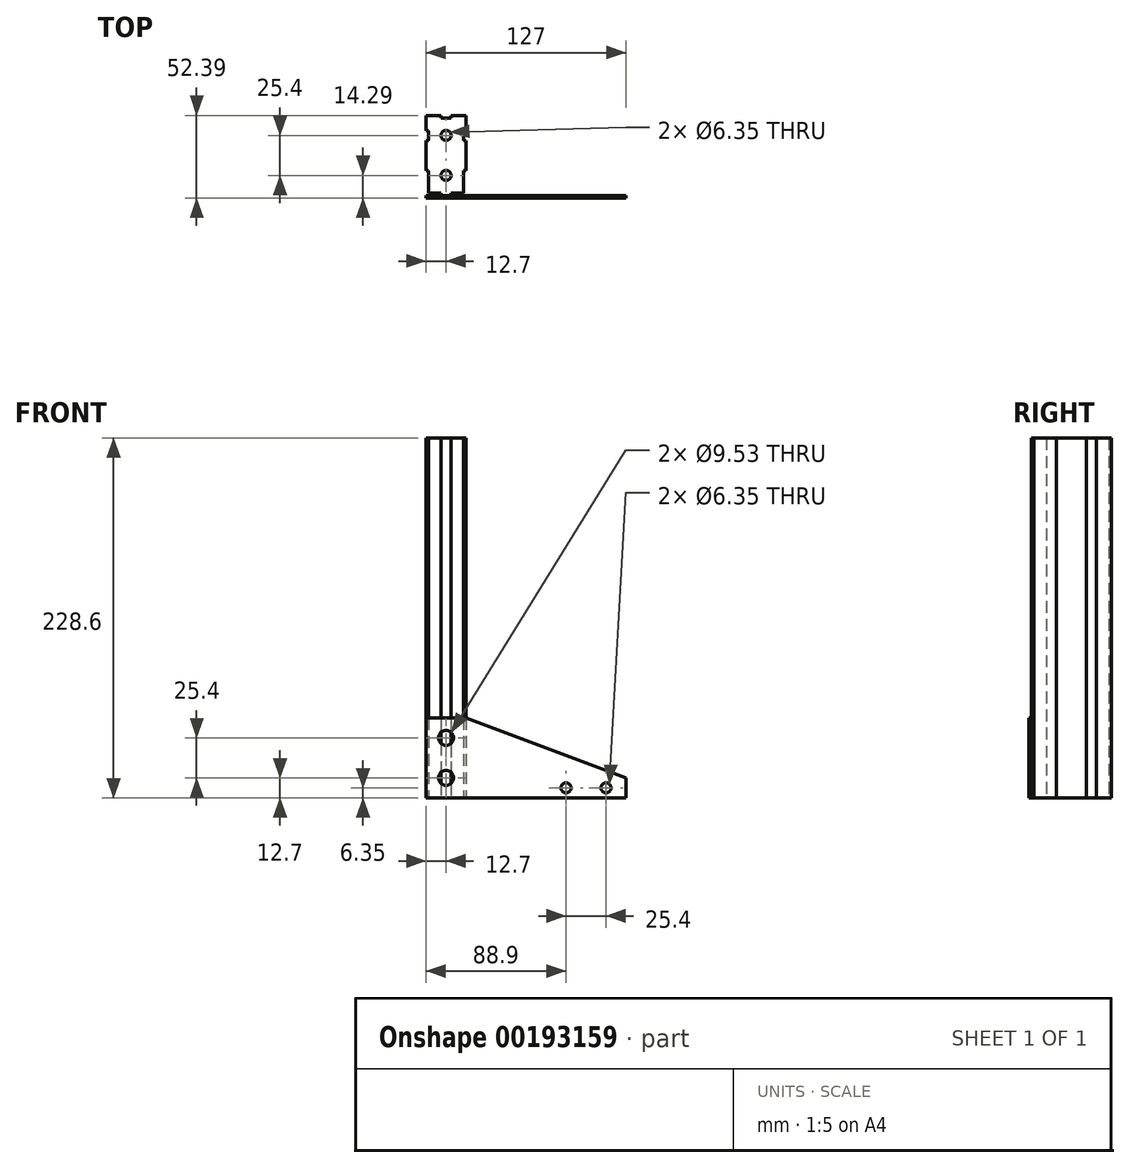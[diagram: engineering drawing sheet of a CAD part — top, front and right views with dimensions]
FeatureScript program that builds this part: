
annotation { "Feature Type Name" : "Feature", "Feature Type Description" : "" }
export const myFeature = defineFeature(function(context is Context, id is Id, definition is map)
    precondition{}
    {
        {
            var Q0;
            Q0=qCreatedBy(makeId("Top.planeOp"),FACE);
            var sketch = newSketch(context, id + "F0", { "sketchPlane" : qUnion([Q0])});
            skLineSegment(sketch, "E0.bottom", {"start": v(-12.7, -25.4) * mm, "end": v(12.7, -25.4) * mm});
            skLineSegment(sketch, "E0.top", {"start": v(-12.7, 25.4) * mm, "end": v(12.7, 25.4) * mm});
            skLineSegment(sketch, "E0.left", {"start": v(-12.7, -25.4) * mm, "end": v(-12.7, 25.4) * mm});
            skLineSegment(sketch, "E0.right", {"start": v(12.7, -25.4) * mm, "end": v(12.7, 25.4) * mm});
            skPoint(sketch, "E0.middle", {"position": v(0, 0) * mm});
            skLineSegment(sketch, "E1", {"start": v(12.7, 0) * mm, "end": v(88.9, 0) * mm, "construction": true});
            skPoint(sketch, "E1.endSnap0", {"position": v(12.7, 0) * mm});
            skLineSegment(sketch, "E2", {"start": v(88.9, 0) * mm, "end": v(114.3, 0) * mm, "construction": true});
            skLineSegment(sketch, "E3.bottom", {"start": v(79.38, -9.53) * mm, "end": v(98.42, -9.53) * mm});
            skLineSegment(sketch, "E3.top", {"start": v(79.38, 9.52) * mm, "end": v(98.42, 9.52) * mm});
            skLineSegment(sketch, "E3.left", {"start": v(79.38, -9.53) * mm, "end": v(79.38, 9.52) * mm});
            skLineSegment(sketch, "E3.right", {"start": v(98.42, -9.53) * mm, "end": v(98.42, 9.52) * mm});
            skPoint(sketch, "E3.middle", {"position": v(88.9, 0) * mm});
            skLineSegment(sketch, "E4.bottom", {"start": v(63.5, -25.4) * mm, "end": v(114.3, -25.4) * mm});
            skLineSegment(sketch, "E4.top", {"start": v(63.5, 25.4) * mm, "end": v(114.3, 25.4) * mm});
            skLineSegment(sketch, "E4.left", {"start": v(63.5, -25.4) * mm, "end": v(63.5, 25.4) * mm});
            skLineSegment(sketch, "E4.right", {"start": v(114.3, -25.4) * mm, "end": v(114.3, 25.4) * mm});
            skLineSegment(sketch, "E5", {"start": v(-12.7, 0) * mm, "end": v(12.7, 0) * mm});
            skLineSegment(sketch, "E6", {"start": v(0, 25.4) * mm, "end": v(0, 0) * mm});
            skLineSegment(sketch, "E7", {"start": v(0, 0) * mm, "end": v(0, -25.4) * mm});
            skCircle(sketch, "E8", {"center": v(0, 12.7) * mm, "radius": 3.18 * mm});
            skCircle(sketch, "E9", {"center": v(0, -12.7) * mm, "radius": 3.18 * mm});
            skLineSegment(sketch, "E10.bottom", {"start": v(-11.11, 1.59) * mm, "end": v(11.11, 1.59) * mm});
            skLineSegment(sketch, "E10.top", {"start": v(-11.11, 23.81) * mm, "end": v(11.11, 23.81) * mm});
            skLineSegment(sketch, "E10.left", {"start": v(-11.11, 1.59) * mm, "end": v(-11.11, 23.81) * mm});
            skLineSegment(sketch, "E10.right", {"start": v(11.11, 1.59) * mm, "end": v(11.11, 23.81) * mm});
            skLineSegment(sketch, "E11.bottom", {"start": v(-11.11, -23.81) * mm, "end": v(11.11, -23.81) * mm});
            skLineSegment(sketch, "E11.top", {"start": v(-11.11, -1.59) * mm, "end": v(11.11, -1.59) * mm});
            skLineSegment(sketch, "E11.left", {"start": v(-11.11, -23.81) * mm, "end": v(-11.11, -1.59) * mm});
            skLineSegment(sketch, "E11.right", {"start": v(11.11, -23.81) * mm, "end": v(11.11, -1.59) * mm});
            skLineSegment(sketch, "E12.bottom", {"start": v(-3.18, -25.4) * mm, "end": v(3.18, -25.4) * mm});
            skLineSegment(sketch, "E12.top", {"start": v(-3.18, 25.4) * mm, "end": v(3.18, 25.4) * mm});
            skLineSegment(sketch, "E12.left", {"start": v(-3.18, -25.4) * mm, "end": v(-3.18, 25.4) * mm});
            skLineSegment(sketch, "E12.right", {"start": v(3.18, -25.4) * mm, "end": v(3.18, 25.4) * mm});
            skLineSegment(sketch, "E13.bottom", {"start": v(-12.7, 9.53) * mm, "end": v(12.7, 9.53) * mm});
            skLineSegment(sketch, "E13.top", {"start": v(-12.7, 15.88) * mm, "end": v(12.7, 15.88) * mm});
            skLineSegment(sketch, "E13.left", {"start": v(-12.7, 9.53) * mm, "end": v(-12.7, 15.88) * mm});
            skLineSegment(sketch, "E13.right", {"start": v(12.7, 9.53) * mm, "end": v(12.7, 15.88) * mm});
            skLineSegment(sketch, "E14.MirrorCS", {"start": v(12.7, -9.53) * mm, "end": v(12.7, -15.88) * mm});
            skLineSegment(sketch, "E15.MirrorCS", {"start": v(-12.7, -9.52) * mm, "end": v(12.7, -9.53) * mm});
            skLineSegment(sketch, "E16.MirrorCS", {"start": v(-12.7, -15.88) * mm, "end": v(12.7, -15.88) * mm});
            skLineSegment(sketch, "E17.MirrorCS", {"start": v(-12.7, -9.52) * mm, "end": v(-12.7, -15.88) * mm});
            skSolve(sketch);
        }
        {
            var Q0;
            Q0=makeQuery(id+"F0.imprint","IMPRINT",FACE,{"disambiguationData":[TD([[makeQuery(id+"F0.imprint","IMPRINT",EDGE,{"derivedFrom":sQuery(id+"F0.wireOp",EDGE,"E0.bottom")}),1.0]])]});
            var Q1;
            {var subQ7=sQuery(id+"F0.wireOp",EDGE,"E5");var subQ8=sQuery(id+"F0.wireOp",EDGE,"E0.right");var subQ9=makeQuery(id+"F0.imprint","INTERSECT",VERTEX,{"derivedFrom":[subQ8,subQ7]});Q1=makeQuery(id+"F0.imprint","IMPRINT",FACE,{"disambiguationData":[TD([[makeQuery(id+"F0.imprint","IMPRINT",EDGE,{"disambiguationData":[TD([[subQ9,1.0]])],"derivedFrom":subQ7}),-1.0]])]});}
            var Q2;
            {var subQ6=sQuery(id+"F0.wireOp",EDGE,"E5");var subQ9=sQuery(id+"F0.wireOp",EDGE,"E0.left");var subQ10=makeQuery(id+"F0.imprint","INTERSECT",VERTEX,{"derivedFrom":[subQ9,subQ6]});Q2=makeQuery(id+"F0.imprint","IMPRINT",FACE,{"disambiguationData":[TD([[makeQuery(id+"F0.imprint","IMPRINT",EDGE,{"disambiguationData":[TD([[subQ10,-1.0]])],"derivedFrom":subQ6}),-1.0]])]});}
            var Q3;
            {var subQ7=sQuery(id+"F0.wireOp",EDGE,"E5");var subQ8=sQuery(id+"F0.wireOp",EDGE,"E0.left");var subQ9=makeQuery(id+"F0.imprint","INTERSECT",VERTEX,{"derivedFrom":[subQ8,subQ7]});Q3=makeQuery(id+"F0.imprint","IMPRINT",FACE,{"disambiguationData":[TD([[makeQuery(id+"F0.imprint","IMPRINT",EDGE,{"disambiguationData":[TD([[subQ9,-1.0]])],"derivedFrom":subQ7}),1.0]])]});}
            var Q4;
            {var subQ0=sQuery(id+"F0.wireOp",EDGE,"E6");var subQ5=sQuery(id+"F0.wireOp",EDGE,"E10.bottom");var subQ6=makeQuery(id+"F0.imprint","INTERSECT",VERTEX,{"derivedFrom":[subQ0,subQ5]});Q4=makeQuery(id+"F0.imprint","IMPRINT",FACE,{"disambiguationData":[TD([[makeQuery(id+"F0.imprint","IMPRINT",EDGE,{"disambiguationData":[TD([[subQ6,-1.0]])],"derivedFrom":subQ5}),-1.0]])]});}
            var Q5;
            {var subQ0=sQuery(id+"F0.wireOp",EDGE,"E6");var subQ5=sQuery(id+"F0.wireOp",EDGE,"E10.bottom");var subQ6=makeQuery(id+"F0.imprint","INTERSECT",VERTEX,{"derivedFrom":[subQ0,subQ5]});Q5=makeQuery(id+"F0.imprint","IMPRINT",FACE,{"disambiguationData":[TD([[makeQuery(id+"F0.imprint","IMPRINT",EDGE,{"disambiguationData":[TD([[subQ6,1.0]])],"derivedFrom":subQ5}),-1.0]])]});}
            var Q6;
            {var subQ0=sQuery(id+"F0.wireOp",EDGE,"E7");var subQ5=sQuery(id+"F0.wireOp",EDGE,"E11.top");var subQ6=makeQuery(id+"F0.imprint","INTERSECT",VERTEX,{"derivedFrom":[subQ0,subQ5]});Q6=makeQuery(id+"F0.imprint","IMPRINT",FACE,{"disambiguationData":[TD([[makeQuery(id+"F0.imprint","IMPRINT",EDGE,{"disambiguationData":[TD([[subQ6,1.0]])],"derivedFrom":subQ5}),1.0]])]});}
            var Q7;
            {var subQ0=sQuery(id+"F0.wireOp",EDGE,"E7");var subQ5=sQuery(id+"F0.wireOp",EDGE,"E11.top");var subQ7=makeQuery(id+"F0.imprint","INTERSECT",VERTEX,{"derivedFrom":[subQ0,subQ5]});Q7=makeQuery(id+"F0.imprint","IMPRINT",FACE,{"disambiguationData":[TD([[makeQuery(id+"F0.imprint","IMPRINT",EDGE,{"disambiguationData":[TD([[subQ7,-1.0]])],"derivedFrom":subQ5}),1.0]])]});}
            var Q8;
            {var subQ5=sQuery(id+"F0.wireOp",EDGE,"E5");var subQ6=sQuery(id+"F0.wireOp",EDGE,"E0.right");var subQ7=makeQuery(id+"F0.imprint","INTERSECT",VERTEX,{"derivedFrom":[subQ6,subQ5]});Q8=makeQuery(id+"F0.imprint","IMPRINT",FACE,{"disambiguationData":[TD([[makeQuery(id+"F0.imprint","IMPRINT",EDGE,{"disambiguationData":[TD([[subQ7,1.0]])],"derivedFrom":subQ5}),1.0]])]});}
            var Q9;
            {var subQ0=sQuery(id+"F0.wireOp",EDGE,"E10.right");var subQ1=sQuery(id+"F0.wireOp",EDGE,"E10.bottom");var subQ2=makeQuery(id+"F0.imprint","INTERSECT",VERTEX,{"derivedFrom":[subQ1,subQ0]});Q9=makeQuery(id+"F0.imprint","IMPRINT",FACE,{"disambiguationData":[TD([[makeQuery(id+"F0.imprint","IMPRINT",EDGE,{"disambiguationData":[TD([[subQ2,1.0]])],"derivedFrom":subQ1}),1.0]])]});}
            var Q10;
            {var subQ0=sQuery(id+"F0.wireOp",EDGE,"E10.left");var subQ1=sQuery(id+"F0.wireOp",EDGE,"E10.bottom");var subQ2=makeQuery(id+"F0.imprint","INTERSECT",VERTEX,{"derivedFrom":[subQ1,subQ0]});Q10=makeQuery(id+"F0.imprint","IMPRINT",FACE,{"disambiguationData":[TD([[makeQuery(id+"F0.imprint","IMPRINT",EDGE,{"disambiguationData":[TD([[subQ2,-1.0]])],"derivedFrom":subQ1}),1.0]])]});}
            var Q11;
            {var subQ0=sQuery(id+"F0.wireOp",EDGE,"E11.left");var subQ1=sQuery(id+"F0.wireOp",EDGE,"E11.top");var subQ2=makeQuery(id+"F0.imprint","INTERSECT",VERTEX,{"derivedFrom":[subQ1,subQ0]});Q11=makeQuery(id+"F0.imprint","IMPRINT",FACE,{"disambiguationData":[TD([[makeQuery(id+"F0.imprint","IMPRINT",EDGE,{"disambiguationData":[TD([[subQ2,-1.0]])],"derivedFrom":subQ1}),-1.0]])]});}
            var Q12;
            {var subQ0=sQuery(id+"F0.wireOp",EDGE,"E11.right");var subQ1=sQuery(id+"F0.wireOp",EDGE,"E11.top");var subQ2=makeQuery(id+"F0.imprint","INTERSECT",VERTEX,{"derivedFrom":[subQ1,subQ0]});Q12=makeQuery(id+"F0.imprint","IMPRINT",FACE,{"disambiguationData":[TD([[makeQuery(id+"F0.imprint","IMPRINT",EDGE,{"disambiguationData":[TD([[subQ2,1.0]])],"derivedFrom":subQ1}),-1.0]])]});}
            var Q13;
            {var subQ0=sQuery(id+"F0.wireOp",EDGE,"E11.left");var subQ1=sQuery(id+"F0.wireOp",EDGE,"E11.bottom");var subQ2=makeQuery(id+"F0.imprint","INTERSECT",VERTEX,{"derivedFrom":[subQ1,subQ0]});Q13=makeQuery(id+"F0.imprint","IMPRINT",FACE,{"disambiguationData":[TD([[makeQuery(id+"F0.imprint","IMPRINT",EDGE,{"disambiguationData":[TD([[subQ2,-1.0]])],"derivedFrom":subQ1}),1.0]])]});}
            var Q14;
            {var subQ0=sQuery(id+"F0.wireOp",EDGE,"E11.right");var subQ1=sQuery(id+"F0.wireOp",EDGE,"E11.bottom");var subQ2=makeQuery(id+"F0.imprint","INTERSECT",VERTEX,{"derivedFrom":[subQ1,subQ0]});Q14=makeQuery(id+"F0.imprint","IMPRINT",FACE,{"disambiguationData":[TD([[makeQuery(id+"F0.imprint","IMPRINT",EDGE,{"disambiguationData":[TD([[subQ2,1.0]])],"derivedFrom":subQ1}),1.0]])]});}
            var Q15;
            {var subQ0=sQuery(id+"F0.wireOp",EDGE,"E10.left");var subQ1=sQuery(id+"F0.wireOp",EDGE,"E10.top");var subQ2=makeQuery(id+"F0.imprint","INTERSECT",VERTEX,{"derivedFrom":[subQ1,subQ0]});Q15=makeQuery(id+"F0.imprint","IMPRINT",FACE,{"disambiguationData":[TD([[makeQuery(id+"F0.imprint","IMPRINT",EDGE,{"disambiguationData":[TD([[subQ2,-1.0]])],"derivedFrom":subQ1}),-1.0]])]});}
            var Q16;
            {var subQ0=sQuery(id+"F0.wireOp",EDGE,"E10.right");var subQ1=sQuery(id+"F0.wireOp",EDGE,"E10.top");var subQ2=makeQuery(id+"F0.imprint","INTERSECT",VERTEX,{"derivedFrom":[subQ1,subQ0]});Q16=makeQuery(id+"F0.imprint","IMPRINT",FACE,{"disambiguationData":[TD([[makeQuery(id+"F0.imprint","IMPRINT",EDGE,{"disambiguationData":[TD([[subQ2,1.0]])],"derivedFrom":subQ1}),1.0]])]});}
            var Q17;
            {var subQ0=sQuery(id+"F0.wireOp",EDGE,"E10.right");var subQ1=sQuery(id+"F0.wireOp",EDGE,"E10.top");var subQ2=makeQuery(id+"F0.imprint","INTERSECT",VERTEX,{"derivedFrom":[subQ1,subQ0]});Q17=makeQuery(id+"F0.imprint","IMPRINT",FACE,{"disambiguationData":[TD([[makeQuery(id+"F0.imprint","IMPRINT",EDGE,{"disambiguationData":[TD([[subQ2,1.0]])],"derivedFrom":subQ1}),-1.0]])]});}
            var Q18;
            {var subQ0=sQuery(id+"F0.wireOp",EDGE,"E10.left");var subQ1=sQuery(id+"F0.wireOp",EDGE,"E10.top");var subQ2=makeQuery(id+"F0.imprint","INTERSECT",VERTEX,{"derivedFrom":[subQ1,subQ0]});Q18=makeQuery(id+"F0.imprint","IMPRINT",FACE,{"disambiguationData":[TD([[makeQuery(id+"F0.imprint","IMPRINT",EDGE,{"disambiguationData":[TD([[subQ2,-1.0]])],"derivedFrom":subQ1}),1.0]])]});}
            var Q19;
            {var subQ0=sQuery(id+"F0.wireOp",EDGE,"E10.top");var subQ1=sQuery(id+"F0.wireOp",EDGE,"E6");var subQ2=makeQuery(id+"F0.imprint","INTERSECT",VERTEX,{"derivedFrom":[subQ1,subQ0]});Q19=makeQuery(id+"F0.imprint","IMPRINT",FACE,{"disambiguationData":[TD([[makeQuery(id+"F0.imprint","IMPRINT",EDGE,{"disambiguationData":[TD([[subQ2,1.0]])],"derivedFrom":subQ0}),-1.0]])]});}
            var Q20;
            {var subQ0=sQuery(id+"F0.wireOp",EDGE,"E10.top");var subQ1=sQuery(id+"F0.wireOp",EDGE,"E6");var subQ2=makeQuery(id+"F0.imprint","INTERSECT",VERTEX,{"derivedFrom":[subQ1,subQ0]});Q20=makeQuery(id+"F0.imprint","IMPRINT",FACE,{"disambiguationData":[TD([[makeQuery(id+"F0.imprint","IMPRINT",EDGE,{"disambiguationData":[TD([[subQ2,-1.0]])],"derivedFrom":subQ0}),-1.0]])]});}
            var Q21;
            {var subQ1=sQuery(id+"F0.wireOp",EDGE,"E11.left");var subQ5=sQuery(id+"F0.wireOp",EDGE,"E16.MirrorCS");var subQ8=makeQuery(id+"F0.imprint","INTERSECT",VERTEX,{"derivedFrom":[subQ1,subQ5]});Q21=makeQuery(id+"F0.imprint","IMPRINT",FACE,{"disambiguationData":[TD([[makeQuery(id+"F0.imprint","IMPRINT",EDGE,{"disambiguationData":[TD([[subQ8,-1.0]])],"derivedFrom":subQ1}),-1.0]])]});}
            var Q22;
            {var subQ0=sQuery(id+"F0.wireOp",EDGE,"E9");var subQ1=sQuery(id+"F0.wireOp",EDGE,"E12.left");var subQ2=makeQuery(id+"F0.imprint","INTERSECT",VERTEX,{"derivedFrom":[subQ1,subQ0]});Q22=makeQuery(id+"F0.imprint","IMPRINT",FACE,{"disambiguationData":[TD([[makeQuery(id+"F0.imprint","IMPRINT",EDGE,{"disambiguationData":[TD([[subQ2,-1.0]])],"derivedFrom":subQ1}),-1.0]])]});}
            var Q23;
            {var subQ0=sQuery(id+"F0.wireOp",EDGE,"E11.top");var subQ1=sQuery(id+"F0.wireOp",EDGE,"E7");var subQ2=makeQuery(id+"F0.imprint","INTERSECT",VERTEX,{"derivedFrom":[subQ1,subQ0]});Q23=makeQuery(id+"F0.imprint","IMPRINT",FACE,{"disambiguationData":[TD([[makeQuery(id+"F0.imprint","IMPRINT",EDGE,{"disambiguationData":[TD([[subQ2,1.0]])],"derivedFrom":subQ0}),-1.0]])]});}
            var Q24;
            {var subQ0=sQuery(id+"F0.wireOp",EDGE,"E11.top");var subQ1=sQuery(id+"F0.wireOp",EDGE,"E7");var subQ2=makeQuery(id+"F0.imprint","INTERSECT",VERTEX,{"derivedFrom":[subQ1,subQ0]});Q24=makeQuery(id+"F0.imprint","IMPRINT",FACE,{"disambiguationData":[TD([[makeQuery(id+"F0.imprint","IMPRINT",EDGE,{"disambiguationData":[TD([[subQ2,-1.0]])],"derivedFrom":subQ0}),-1.0]])]});}
            var Q25;
            {var subQ0=sQuery(id+"F0.wireOp",EDGE,"E9");var subQ1=sQuery(id+"F0.wireOp",EDGE,"E12.right");var subQ2=makeQuery(id+"F0.imprint","INTERSECT",VERTEX,{"derivedFrom":[subQ1,subQ0]});Q25=makeQuery(id+"F0.imprint","IMPRINT",FACE,{"disambiguationData":[TD([[makeQuery(id+"F0.imprint","IMPRINT",EDGE,{"disambiguationData":[TD([[subQ2,-1.0]])],"derivedFrom":subQ1}),1.0]])]});}
            var Q26;
            {var subQ1=sQuery(id+"F0.wireOp",EDGE,"E11.right");var subQ6=sQuery(id+"F0.wireOp",EDGE,"E16.MirrorCS");var subQ8=makeQuery(id+"F0.imprint","INTERSECT",VERTEX,{"derivedFrom":[subQ1,subQ6]});Q26=makeQuery(id+"F0.imprint","IMPRINT",FACE,{"disambiguationData":[TD([[makeQuery(id+"F0.imprint","IMPRINT",EDGE,{"disambiguationData":[TD([[subQ8,-1.0]])],"derivedFrom":subQ1}),1.0]])]});}
            var Q27;
            {var subQ0=sQuery(id+"F0.wireOp",EDGE,"E11.bottom");var subQ1=sQuery(id+"F0.wireOp",EDGE,"E7");var subQ2=makeQuery(id+"F0.imprint","INTERSECT",VERTEX,{"derivedFrom":[subQ1,subQ0]});Q27=makeQuery(id+"F0.imprint","IMPRINT",FACE,{"disambiguationData":[TD([[makeQuery(id+"F0.imprint","IMPRINT",EDGE,{"disambiguationData":[TD([[subQ2,-1.0]])],"derivedFrom":subQ0}),1.0]])]});}
            var Q28;
            {var subQ0=sQuery(id+"F0.wireOp",EDGE,"E11.bottom");var subQ1=sQuery(id+"F0.wireOp",EDGE,"E7");var subQ2=makeQuery(id+"F0.imprint","INTERSECT",VERTEX,{"derivedFrom":[subQ1,subQ0]});Q28=makeQuery(id+"F0.imprint","IMPRINT",FACE,{"disambiguationData":[TD([[makeQuery(id+"F0.imprint","IMPRINT",EDGE,{"disambiguationData":[TD([[subQ2,1.0]])],"derivedFrom":subQ0}),1.0]])]});}
            var Q29;
            {var subQ0=sQuery(id+"F0.wireOp",EDGE,"E16.MirrorCS");var subQ1=sQuery(id+"F0.wireOp",EDGE,"E12.left");var subQ2=makeQuery(id+"F0.imprint","INTERSECT",VERTEX,{"derivedFrom":[subQ1,subQ0]});Q29=makeQuery(id+"F0.imprint","IMPRINT",FACE,{"disambiguationData":[TD([[makeQuery(id+"F0.imprint","IMPRINT",EDGE,{"disambiguationData":[TD([[subQ2,-1.0]])],"derivedFrom":subQ1}),-1.0]])]});}
            var Q30;
            {var subQ0=sQuery(id+"F0.wireOp",EDGE,"E13.bottom");var subQ1=sQuery(id+"F0.wireOp",EDGE,"E10.left");var subQ2=makeQuery(id+"F0.imprint","INTERSECT",VERTEX,{"derivedFrom":[subQ1,subQ0]});Q30=makeQuery(id+"F0.imprint","IMPRINT",FACE,{"disambiguationData":[TD([[makeQuery(id+"F0.imprint","IMPRINT",EDGE,{"disambiguationData":[TD([[subQ2,-1.0]])],"derivedFrom":subQ1}),-1.0]])]});}
            var Q31;
            {var subQ0=sQuery(id+"F0.wireOp",EDGE,"E12.left");var subQ1=sQuery(id+"F0.wireOp",EDGE,"E8");var subQ2=makeQuery(id+"F0.imprint","INTERSECT",VERTEX,{"derivedFrom":[subQ1,subQ0]});Q31=makeQuery(id+"F0.imprint","IMPRINT",FACE,{"disambiguationData":[TD([[makeQuery(id+"F0.imprint","IMPRINT",EDGE,{"disambiguationData":[TD([[subQ2,1.0]])],"derivedFrom":subQ0}),-1.0]])]});}
            var Q32;
            {var subQ0=sQuery(id+"F0.wireOp",EDGE,"E12.right");var subQ1=sQuery(id+"F0.wireOp",EDGE,"E8");var subQ2=makeQuery(id+"F0.imprint","INTERSECT",VERTEX,{"derivedFrom":[subQ1,subQ0]});Q32=makeQuery(id+"F0.imprint","IMPRINT",FACE,{"disambiguationData":[TD([[makeQuery(id+"F0.imprint","IMPRINT",EDGE,{"disambiguationData":[TD([[subQ2,1.0]])],"derivedFrom":subQ0}),1.0]])]});}
            var Q33;
            {var subQ0=sQuery(id+"F0.wireOp",EDGE,"E12.right");var subQ1=sQuery(id+"F0.wireOp",EDGE,"E8");var subQ2=makeQuery(id+"F0.imprint","INTERSECT",VERTEX,{"derivedFrom":[subQ1,subQ0]});Q33=makeQuery(id+"F0.imprint","IMPRINT",FACE,{"disambiguationData":[TD([[makeQuery(id+"F0.imprint","IMPRINT",EDGE,{"disambiguationData":[TD([[subQ2,-1.0]])],"derivedFrom":subQ0}),1.0]])]});}
            var Q34;
            {var subQ0=sQuery(id+"F0.wireOp",EDGE,"E12.left");var subQ1=sQuery(id+"F0.wireOp",EDGE,"E8");var subQ2=makeQuery(id+"F0.imprint","INTERSECT",VERTEX,{"derivedFrom":[subQ1,subQ0]});Q34=makeQuery(id+"F0.imprint","IMPRINT",FACE,{"disambiguationData":[TD([[makeQuery(id+"F0.imprint","IMPRINT",EDGE,{"disambiguationData":[TD([[subQ2,-1.0]])],"derivedFrom":subQ0}),-1.0]])]});}
            var Q35;
            {var subQ0=sQuery(id+"F0.wireOp",EDGE,"E13.bottom");var subQ1=sQuery(id+"F0.wireOp",EDGE,"E10.right");var subQ2=makeQuery(id+"F0.imprint","INTERSECT",VERTEX,{"derivedFrom":[subQ1,subQ0]});Q35=makeQuery(id+"F0.imprint","IMPRINT",FACE,{"disambiguationData":[TD([[makeQuery(id+"F0.imprint","IMPRINT",EDGE,{"disambiguationData":[TD([[subQ2,-1.0]])],"derivedFrom":subQ1}),1.0]])]});}
            var Q36;
            {var subQ0=sQuery(id+"F0.wireOp",EDGE,"E10.bottom");var subQ1=sQuery(id+"F0.wireOp",EDGE,"E6");var subQ2=makeQuery(id+"F0.imprint","INTERSECT",VERTEX,{"derivedFrom":[subQ1,subQ0]});Q36=makeQuery(id+"F0.imprint","IMPRINT",FACE,{"disambiguationData":[TD([[makeQuery(id+"F0.imprint","IMPRINT",EDGE,{"disambiguationData":[TD([[subQ2,1.0]])],"derivedFrom":subQ0}),1.0]])]});}
            var Q37;
            {var subQ0=sQuery(id+"F0.wireOp",EDGE,"E10.bottom");var subQ1=sQuery(id+"F0.wireOp",EDGE,"E6");var subQ2=makeQuery(id+"F0.imprint","INTERSECT",VERTEX,{"derivedFrom":[subQ1,subQ0]});Q37=makeQuery(id+"F0.imprint","IMPRINT",FACE,{"disambiguationData":[TD([[makeQuery(id+"F0.imprint","IMPRINT",EDGE,{"disambiguationData":[TD([[subQ2,-1.0]])],"derivedFrom":subQ0}),1.0]])]});}
            var Q38;
            {var subQ0=sQuery(id+"F0.wireOp",EDGE,"E16.MirrorCS");var subQ1=sQuery(id+"F0.wireOp",EDGE,"E12.right");var subQ2=makeQuery(id+"F0.imprint","INTERSECT",VERTEX,{"derivedFrom":[subQ1,subQ0]});Q38=makeQuery(id+"F0.imprint","IMPRINT",FACE,{"disambiguationData":[TD([[makeQuery(id+"F0.imprint","IMPRINT",EDGE,{"disambiguationData":[TD([[subQ2,-1.0]])],"derivedFrom":subQ1}),1.0]])]});}
            extrude(context, id + "F1", {"entities" : qUnion([Q0, Q1, Q2, Q3, Q4, Q5, Q6, Q7, Q8, Q9, Q10, Q11, Q12, Q13, Q14, Q15, Q16, Q17, Q18, Q19, Q20, Q21, Q22, Q23, Q24, Q25, Q26, Q27, Q28, Q29, Q30, Q31, Q32, Q33, Q34, Q35, Q36, Q37, Q38]), "depth" : 228.6 * mm});
        }
        {
            var Q0;
            Q0=makeQuery(id+"F0.imprint","IMPRINT",FACE,{"disambiguationData":[TD([[makeQuery(id+"F0.imprint","IMPRINT",EDGE,{"derivedFrom":sQuery(id+"F0.wireOp",EDGE,"E3.bottom")}),-1.0]])]});
            extrude(context, id + "F2", {"entities" : qUnion([Q0]), "depth" : 12.7 * mm});
        }
        {
            var Q0;
            Q0=makeQuery(id+"F1.opExtrude","SWEPT_FACE",FACE,{"disambiguationData":[OSD([sQuery(id+"F0.wireOp",EDGE,"E0.bottom")])]});
            var sketch = newSketch(context, id + "F3", { "sketchPlane" : qUnion([Q0])});
            skLineSegment(sketch, "E18", {"start": v(-12.7, 0) * mm, "end": v(-12.7, 50.8) * mm});
            skLineSegment(sketch, "E19", {"start": v(-12.7, 50.8) * mm, "end": v(12.7, 50.8) * mm});
            skLineSegment(sketch, "E20", {"start": v(-12.7, 60.33) * mm, "end": v(114.3, 12.7) * mm});
            skLineSegment(sketch, "E21", {"start": v(114.3, 12.7) * mm, "end": v(114.3, 0) * mm});
            skLineSegment(sketch, "E22", {"start": v(114.3, 0) * mm, "end": v(-12.7, 0) * mm});
            skLineSegment(sketch, "E23", {"start": v(114.3, 12.7) * mm, "end": v(63.5, 12.7) * mm});
            skLineSegment(sketch, "E24", {"start": v(63.5, 0) * mm, "end": v(63.5, 12.7) * mm});
            skLineSegment(sketch, "E25", {"start": v(12.7, 0) * mm, "end": v(63.5, 0) * mm});
            skLineSegment(sketch, "E26", {"start": v(12.7, 50.8) * mm, "end": v(12.7, 0) * mm});
            skLineSegment(sketch, "E27", {"start": v(0, 50.8) * mm, "end": v(0, 0) * mm, "construction": true});
            skLineSegment(sketch, "E28", {"start": v(-12.7, 38.1) * mm, "end": v(12.7, 38.1) * mm, "construction": true});
            skLineSegment(sketch, "E29", {"start": v(-12.7, 12.7) * mm, "end": v(12.7, 12.7) * mm, "construction": true});
            skCircle(sketch, "E30", {"center": v(0, 38.1) * mm, "radius": 4.76 * mm});
            skCircle(sketch, "E31", {"center": v(0, 12.7) * mm, "radius": 4.76 * mm});
            skLineSegment(sketch, "E32", {"start": v(63.5, 6.35) * mm, "end": v(114.3, 6.35) * mm, "construction": true});
            skLineSegment(sketch, "E33", {"start": v(76.2, 12.7) * mm, "end": v(76.2, 0) * mm, "construction": true});
            skLineSegment(sketch, "E34", {"start": v(101.6, 12.7) * mm, "end": v(101.6, 0) * mm, "construction": true});
            skCircle(sketch, "E35", {"center": v(76.2, 6.35) * mm, "radius": 3.18 * mm});
            skCircle(sketch, "E36", {"center": v(101.6, 6.35) * mm, "radius": 3.18 * mm});
            skLineSegment(sketch, "E37", {"start": v(-12.7, 50.8) * mm, "end": v(-12.7, 95.25) * mm, "construction": true});
            skLineSegment(sketch, "E38", {"start": v(-12.7, 60.33) * mm, "end": v(-12.7, 73.03) * mm, "construction": true});
            skLineSegment(sketch, "E39", {"start": v(-12.7, 73.03) * mm, "end": v(114.3, 73.03) * mm, "construction": true});
            skLineSegment(sketch, "E40", {"start": v(114.3, 73.03) * mm, "end": v(114.3, 22.23) * mm, "construction": true});
            skLineSegment(sketch, "E41", {"start": v(114.3, 22.23) * mm, "end": v(88.9, 22.23) * mm, "construction": true});
            skSolve(sketch);
        }
        {
            var Q0;
            Q0 = qSketchRegion(id + "F3", true);
            extrude(context, id + "F4", {"entities" : qUnion([Q0]), "depth" : 1.59 * mm});
        }
        {
            var Q0;
            Q0=makeQuery(id+"F2.opExtrude","SWEPT_BODY",BODY,{"disambiguationData":[OSD([sQuery(id+"F0.wireOp",EDGE,"E3.bottom"),sQuery(id+"F0.wireOp",EDGE,"E3.top"),sQuery(id+"F0.wireOp",EDGE,"E3.left"),sQuery(id+"F0.wireOp",EDGE,"E3.right"),sQuery(id+"F0.wireOp",EDGE,"E4.bottom"),sQuery(id+"F0.wireOp",EDGE,"E4.top"),sQuery(id+"F0.wireOp",EDGE,"E4.left"),sQuery(id+"F0.wireOp",EDGE,"E4.right")])]});
            deleteBodies(context, id + "F5", {"entities" : qUnion([Q0])});
        }
    });
